# Revit family: Towel_Dispenser-C_Fold_Paper-Whitehall-BestCare_DignitySuite-WHD-CF
name_source: partatom
category: Specialty Equipment
revit_build: Autodesk Revit 2018 (Build: 20170223_1515(x64)
units: mm (PartAtom-declared; Revit-internal decimal feet)

## family parameters
Cut with Voids When Loaded = No
Host = Face
OmniClass Number = 23.40.20.21.17
OmniClass Title = Paper Towel Dispensers, Disposal Units
Part Type = Normal
Room Calculation Point = No
Round Connector Dimension = Use Diameter
Shared = Yes

## types (1)
- WHD-CF
    -OCC Optional Corterra Color Specify OCC- = No
    Assembly Code = C1030200
    Default Elevation = 0"
    Description = Ligature Resistant C-Fold Paper Towel Dispenser
    Dispenser Material = Polymer Resin Corterra-Whitehall-Blanco (OCC11)
    Height = 14"
    Installation Type = Wall Mounted
    Length = 12 1/4"
    Manufacturer = Whitehall Mfg.
    Model = WHD-CF
    Mounting Frame Material = Metal-Whitehall-Galvanized Steel
    Price = Prices may vary. Please consult Manufacturer Representative for most up-to-date price list.
    Product Documentation Link = https://www.whitehallmfg.com
    URL = https://www.whitehallmfg.com
    Warranty Documentation Link = https://www.whitehallmfg.com

## geometry (parser evidence)
native form markers: Sweep x3
no freeform markers — native parametric forms only
